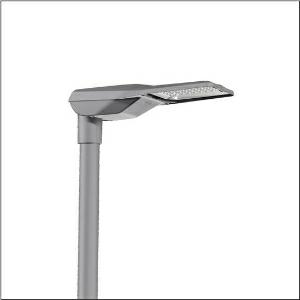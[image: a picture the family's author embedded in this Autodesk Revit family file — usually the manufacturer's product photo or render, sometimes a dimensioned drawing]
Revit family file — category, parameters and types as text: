
# Revit family: streetlight_sl_21_iq_mini___p1_0a_5xe2a41g08hb_15d1
name_source: partatom
category: Lighting Fixtures
units: mm (PartAtom-declared; Revit-internal decimal feet)

## family parameters
Cut with Voids When Loaded = No
Host = Face
Light Source = No
Part Type = Normal
Room Calculation Point = No
Round Connector Dimension = Use Diameter
Shared = No

## types (1)
- --- (1 x LED, 9860 lm, 70.9 W, 4000K)
    Apparent Load = 71 VA
    CIE Flux Codes = 21 50 90 100 100
    Color Rendering = 70
    Color Temperature = 4000K
    Default Elevation = 1800 mm
    Description = Streetlight SL 21 iQ mini, mast luminaire, primary light control with lens, of PMMA, primary optical cover: cover, of toughened safety glass, transparent, light distribution: P1.0a, light emission: direct distribution, primary light characteristic: asymmetric, installation type: post-top, side-entry, LED, High Power LED, rated luminous flux: 9.860lm, luminous efficacy: 139lm/W, light colour: 740, colour temperature: 4000K, control gear: iQ Street-Remote, control: Street-Remote, Auto-Match, Temp-Guard, Lumen-Switch, Night-Set, Smart-Wire, Light-Fading, Desk-Remote (wireless, voltage-free reading and setting of iQ features in the workshop via application-optimized NFC function/RFID function), optimised constant luminous flux control (CLO 2.0), pre-setting: linear dimming characteristic, mains connection: 220..240V, AC, 50/60Hz, start of lifetime: 71W, end of service life: 75W, reduction: 31W, luminaire housing, of diecast aluminium, powder-coated, SITECO metallic grey (DB 702S), corrosivity category C5 high according to DIN EN ISO 12944, please order mast flange separately, inclination adjustable: 0°, 5°, 10°, 15°, sealing non-destructively replaceable, multi-level sealing system, length: 628mm, width: 235mm, height: 110mm, mast flange for spigot size: 42mm (side-entry): 5XC10008XM4, 60/48mm (side-entry/post-top): 5XC10108XM2, 76/60mm (side-entry/post-top): 5XC10108XM1, mounting height: 4..8m, protection rating (complete): IP66, insulation class (complete): insulation class II (safety insulation), certification: CE, ENEC, ENEC+, VDE, impact resistance: IK10, permissible operating ambient temperature for outdoor applications: -40..+50°C, standard-compliant lighting for roads and squares, packaging unit: 1 piece

Light Distribution: P1.0a
    Height = 110 mm
    Lamp = 1 x LED
    Lamp Light Flux = 9860 lm
    Lamp Power = 70.9 W
    Lamp count = 1
    Length = 625 mm
    Luminous efficacy = 139 lm/W
    Manufacturer = Siteco
    ModVariant = No
    Model = 5XE2A41G08HB
    Number of Poles = 1
    OnlyDefault = Yes
    Power Factor = 1
    Product Name = Streetlight SL 21 iQ mini | P1.0a
    Product group = mast luminaire | pylon top
    ProductGroupID = 6100
    Protection Class = Protection class II
    Protection Degree = IP 66
    RLX_Detail_Level = 1
    RLX_Emergency_Light_Flux = 0 lm
    RLX_Emergency_Type = 0
    RLX_Emergency_Type_DB = No
    RlxData = <blob elided: 37517 chars, md5=ff130e50>
    Socket = socket
    Standby Power = 0 W
    System Light Flux = 9860 lm
    System Power = 71 W
    Type Comments = factory setting: luminous flux: 100 % | dim-lin: 254 | 711 mA
    Type Image = l_1003519.jpg
    URL = http://relux.com
    VarID = @adj_157071
    Voltage = 0 V
    Weight = 0.00 kg
    Width = 234 mm

## geometry (parser evidence)
native form markers: Blend x4, Sweep x9
no freeform markers — native parametric forms only
